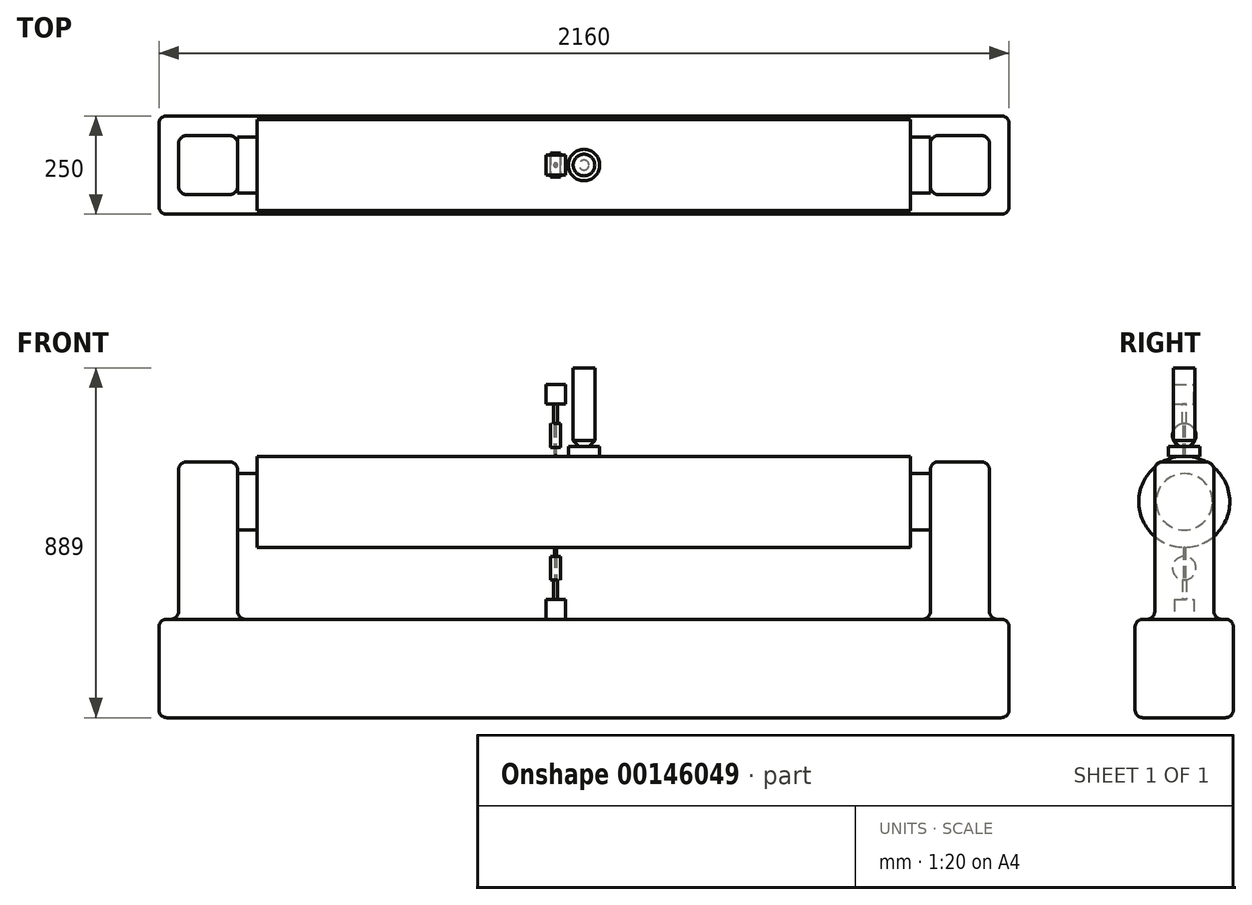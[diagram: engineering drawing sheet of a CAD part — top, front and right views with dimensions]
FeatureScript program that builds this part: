
annotation { "Feature Type Name" : "Feature", "Feature Type Description" : "" }
export const myFeature = defineFeature(function(context is Context, id is Id, definition is map)
    precondition{}
    {
        {
            var Q0;
            Q0=qCreatedBy(makeId("Top.planeOp"),FACE);
            var sketch = newSketch(context, id + "F0", { "sketchPlane" : qUnion([Q0])});
            skLineSegment(sketch, "E0.bottom", {"start": v(1080, -125) * mm, "end": v(-1080, -125) * mm});
            skLineSegment(sketch, "E0.top", {"start": v(1080, 125) * mm, "end": v(-1080, 125) * mm});
            skLineSegment(sketch, "E0.left", {"start": v(1080, -125) * mm, "end": v(1080, 125) * mm});
            skLineSegment(sketch, "E0.right", {"start": v(-1080, -125) * mm, "end": v(-1080, 125) * mm});
            skPoint(sketch, "E0.middle", {"position": v(0, 0) * mm});
            skSolve(sketch);
        }
        {
            var Q0;
            Q0=qSketchRegion(id+"F0",true);
            extrude(context, id + "F1", {"entities" : qUnion([Q0]), "depth" : 250 * mm});
        }
        {
            var Q0;
            Q0=makeQuery(id+"F1.opExtrude","CAP_FACE",FACE,{"disambiguationData":[OSD([sQuery(id+"F0.wireOp",EDGE,"E0.bottom"),sQuery(id+"F0.wireOp",EDGE,"E0.top"),sQuery(id+"F0.wireOp",EDGE,"E0.left"),sQuery(id+"F0.wireOp",EDGE,"E0.right")])],"isStart":false});
            var sketch = newSketch(context, id + "F2", { "sketchPlane" : qUnion([Q0])});
            skLineSegment(sketch, "E1.bottom", {"start": v(-1030, 75) * mm, "end": v(-880, 75) * mm});
            skLineSegment(sketch, "E1.top", {"start": v(-1030, -75) * mm, "end": v(-880, -75) * mm});
            skLineSegment(sketch, "E1.left", {"start": v(-1030, 75) * mm, "end": v(-1030, -75) * mm});
            skLineSegment(sketch, "E1.right", {"start": v(-880, 75) * mm, "end": v(-880, -75) * mm});
            skLineSegment(sketch, "E2.bottom", {"start": v(880, 75) * mm, "end": v(1030, 75) * mm});
            skLineSegment(sketch, "E2.top", {"start": v(880, -75) * mm, "end": v(1030, -75) * mm});
            skLineSegment(sketch, "E2.left", {"start": v(880, 75) * mm, "end": v(880, -75) * mm});
            skLineSegment(sketch, "E2.right", {"start": v(1030, 75) * mm, "end": v(1030, -75) * mm});
            skLineSegment(sketch, "E3", {"start": v(-1080, 0) * mm, "end": v(-1030, 0) * mm, "construction": true});
            skLineSegment(sketch, "E4", {"start": v(1080, 0) * mm, "end": v(1030, 0) * mm, "construction": true});
            skSolve(sketch);
        }
        {
            var Q0;
            Q0=qSketchRegion(id+"F2",true);
            extrude(context, id + "F3", {"entities" : qUnion([Q0]), "operationType" : NewBodyOperationType.ADD, "depth" : 400 * mm});
        }
        {
            var Q0;
            Q0=makeQuery(id+"F3.opExtrude","SWEPT_FACE",FACE,{"disambiguationData":[OSD([sQuery(id+"F2.wireOp",EDGE,"E1.right")])]});
            var sketch = newSketch(context, id + "F4", { "sketchPlane" : qUnion([Q0])});
            skCircle(sketch, "E5", {"center": v(0, 548.5) * mm, "radius": 71.5 * mm});
            skPoint(sketch, "E6", {"position": v(0, 650) * mm});
            skSolve(sketch);
        }
        {
            var Q0;
            Q0=qSketchRegion(id+"F4",true);
            extrude(context, id + "F5", {"entities" : qUnion([Q0]), "depth" : 50 * mm});
        }
        {
            var Q0;
            Q0=makeQuery(id+"F5.opExtrude","SWEPT_BODY",BODY,{"disambiguationData":[OSD([sQuery(id+"F4.wireOp",EDGE,"E5")])]});
            var Q1;
            Q1=qCreatedBy(makeId("Right.planeOp"),FACE);
            mirror(context, id + "F6", {"entities" : qUnion([Q0]), "mirrorPlane" : qUnion([Q1])});
        }
        {
            var Q0;
            Q0=makeQuery(id+"F1.opExtrude","SWEPT_FACE",FACE,{"disambiguationData":[OSD([sQuery(id+"F0.wireOp",EDGE,"E0.bottom")])]});
            var Q1;
            Q1=makeQuery(id+"F1.opExtrude","CAP_FACE",FACE,{"disambiguationData":[OSD([sQuery(id+"F0.wireOp",EDGE,"E0.bottom"),sQuery(id+"F0.wireOp",EDGE,"E0.top"),sQuery(id+"F0.wireOp",EDGE,"E0.left"),sQuery(id+"F0.wireOp",EDGE,"E0.right")])],"isStart":false});
            var Q2;
            Q2=makeQuery(id+"F1.opExtrude","SWEPT_FACE",FACE,{"disambiguationData":[OSD([sQuery(id+"F0.wireOp",EDGE,"E0.top")])]});
            var Q3;
            Q3=makeQuery(id+"F1.opExtrude","CAP_FACE",FACE,{"disambiguationData":[OSD([sQuery(id+"F0.wireOp",EDGE,"E0.bottom"),sQuery(id+"F0.wireOp",EDGE,"E0.top"),sQuery(id+"F0.wireOp",EDGE,"E0.left"),sQuery(id+"F0.wireOp",EDGE,"E0.right")])],"isStart":true});
            var Q4;
            Q4=makeQuery(id+"F3.opExtrude","SWEPT_FACE",FACE,{"disambiguationData":[OSD([sQuery(id+"F2.wireOp",EDGE,"E2.top")])]});
            var Q5;
            Q5=makeQuery(id+"F3.opExtrude","SWEPT_FACE",FACE,{"disambiguationData":[OSD([sQuery(id+"F2.wireOp",EDGE,"E2.right")])]});
            var Q6;
            Q6=makeQuery(id+"F3.opExtrude","SWEPT_FACE",FACE,{"disambiguationData":[OSD([sQuery(id+"F2.wireOp",EDGE,"E2.bottom")])]});
            var Q7;
            Q7=makeQuery(id+"F3.opExtrude","CAP_FACE",FACE,{"disambiguationData":[OSD([sQuery(id+"F2.wireOp",EDGE,"E2.bottom"),sQuery(id+"F2.wireOp",EDGE,"E2.top"),sQuery(id+"F2.wireOp",EDGE,"E2.left"),sQuery(id+"F2.wireOp",EDGE,"E2.right")])],"isStart":false});
            var Q8;
            Q8=makeQuery(id+"F3.opExtrude","SWEPT_FACE",FACE,{"disambiguationData":[OSD([sQuery(id+"F2.wireOp",EDGE,"E1.left")])]});
            var Q9;
            Q9=makeQuery(id+"F3.opExtrude","SWEPT_FACE",FACE,{"disambiguationData":[OSD([sQuery(id+"F2.wireOp",EDGE,"E1.top")])]});
            var Q10;
            Q10=makeQuery(id+"F3.opExtrude","CAP_FACE",FACE,{"disambiguationData":[OSD([sQuery(id+"F2.wireOp",EDGE,"E1.bottom"),sQuery(id+"F2.wireOp",EDGE,"E1.top"),sQuery(id+"F2.wireOp",EDGE,"E1.left"),sQuery(id+"F2.wireOp",EDGE,"E1.right")])],"isStart":false});
            var Q11;
            Q11=makeQuery(id+"F3.opExtrude","SWEPT_FACE",FACE,{"disambiguationData":[OSD([sQuery(id+"F2.wireOp",EDGE,"E1.bottom")])]});
            fillet(context, id + "F7", {"entities" : qUnion([Q0, Q1, Q2, Q3, Q4, Q5, Q6, Q7, Q8, Q9, Q10, Q11]), "radius" : 20 * mm, "tangentPropagation" : true, "allowEdgeOverflow" : false});
        }
        {
            var Q0;
            Q0=makeQuery(id+"F5.opExtrude","CAP_FACE",FACE,{"disambiguationData":[OSD([sQuery(id+"F4.wireOp",EDGE,"E5")])],"isStart":false});
            var sketch = newSketch(context, id + "F8", { "sketchPlane" : qUnion([Q0])});
            skCircle(sketch, "E7", {"center": v(0, 548.5) * mm, "radius": 115.61 * mm});
            skSolve(sketch);
        }
        {
            var Q0;
            Q0=qSketchRegion(id+"F8",true);
            extrude(context, id + "F9", {"entities" : qUnion([Q0]), "depth" : 1660 * mm});
        }
        {
            var Q0;
            Q0=makeQuery(id+"F1.opExtrude","CAP_FACE",FACE,{"disambiguationData":[OSD([sQuery(id+"F0.wireOp",EDGE,"E0.bottom"),sQuery(id+"F0.wireOp",EDGE,"E0.top"),sQuery(id+"F0.wireOp",EDGE,"E0.left"),sQuery(id+"F0.wireOp",EDGE,"E0.right")])],"isStart":false});
            var sketch = newSketch(context, id + "F10", { "sketchPlane" : qUnion([Q0])});
            skLineSegment(sketch, "E8.bottom", {"start": v(-97, -25) * mm, "end": v(-47, -25) * mm});
            skLineSegment(sketch, "E8.top", {"start": v(-97, 25) * mm, "end": v(-47, 25) * mm});
            skLineSegment(sketch, "E8.left", {"start": v(-97, -25) * mm, "end": v(-97, 25) * mm});
            skLineSegment(sketch, "E8.right", {"start": v(-47, -25) * mm, "end": v(-47, 25) * mm});
            skPoint(sketch, "E8.middle", {"position": v(-72, 0) * mm});
            skLineSegment(sketch, "E9", {"start": v(-72, 0) * mm, "end": v(0, 0) * mm, "construction": true});
            skSolve(sketch);
        }
        {
            var Q0;
            Q0=qSketchRegion(id+"F10",true);
            extrude(context, id + "F11", {"entities" : qUnion([Q0]), "depth" : 50 * mm});
        }
        {
            var Q0;
            Q0=makeQuery(id+"F11.opExtrude","CAP_FACE",FACE,{"disambiguationData":[OSD([sQuery(id+"F10.wireOp",EDGE,"E8.bottom"),sQuery(id+"F10.wireOp",EDGE,"E8.top"),sQuery(id+"F10.wireOp",EDGE,"E8.left"),sQuery(id+"F10.wireOp",EDGE,"E8.right")])],"isStart":false});
            var sketch = newSketch(context, id + "F12", { "sketchPlane" : qUnion([Q0])});
            skCircle(sketch, "E10", {"center": v(-72, 0) * mm, "radius": 5 * mm});
            skLineSegment(sketch, "E11", {"start": v(-97, 25) * mm, "end": v(-47, -25) * mm, "construction": true});
            skSolve(sketch);
        }
        {
            var Q0;
            Q0=qSketchRegion(id+"F12",true);
            extrude(context, id + "F13", {"entities" : qUnion([Q0]), "depth" : 50 * mm});
        }
        {
            var Q0;
            Q0=makeQuery(id+"F1.opExtrude","SWEPT_FACE",FACE,{"disambiguationData":[OSD([sQuery(id+"F0.wireOp",EDGE,"E0.left")])]});
            cPlane(context, id + "F14", {"entities" : qUnion([Q0]), "cplaneType" : CPlaneType.OFFSET, "offset" : (1080 + 72) * mm, "oppositeDirection" : true, "width" : 150 * mm, "height" : 150 * mm});
        }
        {
            var Q0;
            Q0=qCreatedBy(id+"F14.planeOp",FACE);
            var sketch = newSketch(context, id + "F15", { "sketchPlane" : qUnion([Q0])});
            skCircle(sketch, "E12", {"center": v(0, 380) * mm, "radius": 30 * mm});
            skSolve(sketch);
        }
        {
            var Q0;
            Q0=qSketchRegion(id+"F15",true);
            extrude(context, id + "F16", {"entities" : qUnion([Q0]), "operationType" : NewBodyOperationType.ADD, "endBound" : BoundingType.SYMMETRIC, "depth" : 25 * mm});
        }
        {
            var Q0;
            Q0=makeQuery(id+"F13.opExtrude","CAP_FACE",FACE,{"disambiguationData":[OSD([sQuery(id+"F12.wireOp",EDGE,"E10")])],"isStart":false});
            var sketch = newSketch(context, id + "F17", { "sketchPlane" : qUnion([Q0])});
            skCircle(sketch, "E13", {"center": v(-72, 0) * mm, "radius": 2.5 * mm});
            skSolve(sketch);
        }
        {
            var Q0;
            Q0=qSketchRegion(id+"F17",true);
            var Q1;
            Q1=makeQuery(id+"F9.opExtrude","SWEPT_BODY",BODY,{"disambiguationData":[OSD([sQuery(id+"F8.wireOp",EDGE,"E7")])]});
            extrude(context, id + "F18", {"entities" : qUnion([Q0]), "endBound" : BoundingType.UP_TO_BODY, "endBoundEntityBody" : qUnion([Q1]), "depth" : 25 * mm});
        }
        {
            var Q0;
            Q0=makeQuery(id+"F3.opExtrude","CAP_FACE",FACE,{"disambiguationData":[OSD([sQuery(id+"F2.wireOp",EDGE,"E2.bottom"),sQuery(id+"F2.wireOp",EDGE,"E2.top"),sQuery(id+"F2.wireOp",EDGE,"E2.left"),sQuery(id+"F2.wireOp",EDGE,"E2.right")])],"isStart":false});
            cPlane(context, id + "F19", {"entities" : qUnion([Q0]), "cplaneType" : CPlaneType.OFFSET, "offset" : 14 * mm, "width" : 150 * mm, "height" : 150 * mm});
        }
        {
            var Q0;
            Q0=qCreatedBy(id+"F19.planeOp",FACE);
            var sketch = newSketch(context, id + "F20", { "sketchPlane" : qUnion([Q0])});
            skCircle(sketch, "E14", {"center": v(0, 0) * mm, "radius": 40 * mm});
            skSolve(sketch);
        }
        {
            var Q0;
            Q0=qSketchRegion(id+"F20",true);
            extrude(context, id + "F21", {"entities" : qUnion([Q0]), "depth" : 25 * mm});
        }
        {
            var Q0;
            Q0=makeQuery(id+"F21.opExtrude","CAP_FACE",FACE,{"disambiguationData":[OSD([sQuery(id+"F20.wireOp",EDGE,"E14")])],"isStart":false});
            var sketch = newSketch(context, id + "F22", { "sketchPlane" : qUnion([Q0])});
            skCircle(sketch, "E15", {"center": v(0, 0) * mm, "radius": 27.5 * mm});
            skSolve(sketch);
        }
        {
            var Q0;
            Q0=qSketchRegion(id+"F22",true);
            extrude(context, id + "F23", {"entities" : qUnion([Q0]), "depth" : 200 * mm});
        }
        {
            var Q0;
            Q0=makeQuery(id+"F18.opExtrude","CAP_EDGE",EDGE,{"disambiguationData":[OSD([sQuery(id+"F17.wireOp",EDGE,"E13")])],"isStart":false});
            chamfer(context, id + "F24", {"entities" : qUnion([Q0]), "width" : 2 * mm, "tangentPropagation" : true});
        }
        {
            var Q0;
            Q0=makeQuery(id+"F3.opExtrude","CAP_FACE",FACE,{"disambiguationData":[OSD([sQuery(id+"F2.wireOp",EDGE,"E1.bottom"),sQuery(id+"F2.wireOp",EDGE,"E1.top"),sQuery(id+"F2.wireOp",EDGE,"E1.left"),sQuery(id+"F2.wireOp",EDGE,"E1.right")])],"isStart":false});
            cPlane(context, id + "F25", {"entities" : qUnion([Q0]), "cplaneType" : CPlaneType.OFFSET, "offset" : 101.5 * mm, "oppositeDirection" : true, "width" : 150 * mm, "height" : 150 * mm});
        }
        {
            var Q0;
            Q0=makeQuery(id+"F13.opExtrude","SWEPT_BODY",BODY,{"disambiguationData":[OSD([sQuery(id+"F12.wireOp",EDGE,"E10")])]});
            var Q1;
            Q1=makeQuery(id+"F16.opExtrude","SWEPT_BODY",BODY,{"disambiguationData":[OSD([sQuery(id+"F15.wireOp",EDGE,"E12")])]});
            var Q2;
            Q2=makeQuery(id+"F18.opExtrude","SWEPT_BODY",BODY,{"disambiguationData":[OSD([sQuery(id+"F17.wireOp",EDGE,"E13")])]});
            var Q3;
            Q3=makeQuery(id+"F11.opExtrude","SWEPT_BODY",BODY,{"disambiguationData":[OSD([sQuery(id+"F10.wireOp",EDGE,"E8.bottom"),sQuery(id+"F10.wireOp",EDGE,"E8.top"),sQuery(id+"F10.wireOp",EDGE,"E8.left"),sQuery(id+"F10.wireOp",EDGE,"E8.right")])]});
            var Q4;
            Q4=qCreatedBy(id+"F25.planeOp",FACE);
            mirror(context, id + "F26", {"entities" : qUnion([Q0, Q1, Q2, Q3]), "mirrorPlane" : qUnion([Q4])});
        }
        {
            var Q0;
            Q0=makeQuery(id+"F23.opExtrude","CAP_EDGE",EDGE,{"disambiguationData":[OSD([sQuery(id+"F22.wireOp",EDGE,"E15")])],"isStart":true});
            chamfer(context, id + "F27", {"entities" : qUnion([Q0]), "width" : 15 * mm, "tangentPropagation" : true});
        }
    });
